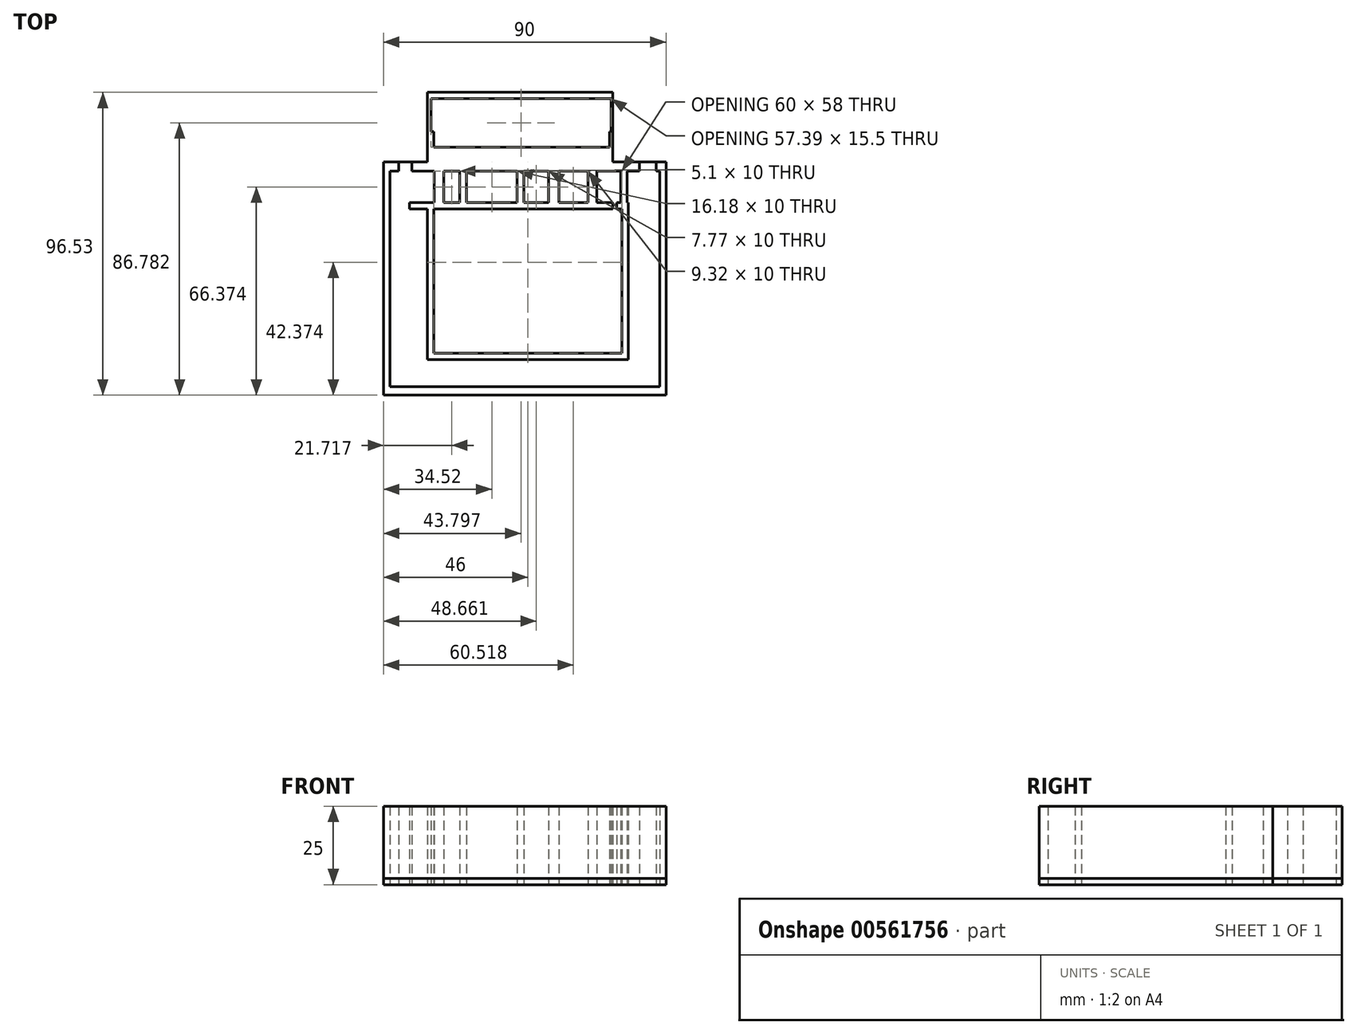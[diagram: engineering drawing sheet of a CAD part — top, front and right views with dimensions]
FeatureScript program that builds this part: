
annotation { "Feature Type Name" : "Feature", "Feature Type Description" : "" }
export const myFeature = defineFeature(function(context is Context, id is Id, definition is map)
    precondition{}
    {
        {
            var Q0;
            Q0=qCreatedBy(makeId("Top.planeOp"),FACE);
            var sketch = newSketch(context, id + "F0", { "sketchPlane" : qUnion([Q0])});
            skLineSegment(sketch, "E0.bottom", {"start": v(-74, 79.03) * mm, "end": v(-62.27, 79.03) * mm, "construction": true});
            skLineSegment(sketch, "E0.top", {"start": v(-62.27, 5.03) * mm, "end": v(-47.4, 5.03) * mm, "construction": true});
            skLineSegment(sketch, "E0.left", {"start": v(-62.27, 79.03) * mm, "end": v(-62.27, 5.03) * mm, "construction": true});
            skLineSegment(sketch, "E1.bottom", {"start": v(-74, 13.37) * mm, "end": v(-14, 13.37) * mm});
            skLineSegment(sketch, "E1.top", {"start": v(-74, 59.37) * mm, "end": v(-22.82, 59.37) * mm});
            skLineSegment(sketch, "E1.left", {"start": v(-74, 13.37) * mm, "end": v(-74, 59.37) * mm});
            skLineSegment(sketch, "E1.right", {"start": v(-14, 13.37) * mm, "end": v(-14, 59.37) * mm});
            skLineSegment(sketch, "E2.bottom", {"start": v(-76, 61.37) * mm, "end": v(-73.89, 61.37) * mm});
            skLineSegment(sketch, "E2.top", {"start": v(-76, 11.37) * mm, "end": v(-12, 11.37) * mm});
            skLineSegment(sketch, "E2.left", {"start": v(-76, 59.37) * mm, "end": v(-76, 11.37) * mm});
            skLineSegment(sketch, "E2.right", {"start": v(-12, 61.37) * mm, "end": v(-12, 11.37) * mm});
            skLineSegment(sketch, "E3", {"start": v(-24.82, 59.37) * mm, "end": v(-24.82, 52.37) * mm});
            skLineSegment(sketch, "E4.top", {"start": v(-32.73, 78.03) * mm, "end": v(-0.73, 78.03) * mm, "construction": true});
            skLineSegment(sketch, "E5", {"start": v(-90, 74.37) * mm, "end": v(-76, 74.37) * mm});
            skLineSegment(sketch, "E6", {"start": v(-74.9, 84.03) * mm, "end": v(-74.9, 94.53) * mm});
            skLineSegment(sketch, "E7", {"start": v(-74.9, 94.53) * mm, "end": v(-17.51, 94.53) * mm});
            skLineSegment(sketch, "E8", {"start": v(-17.51, 94.53) * mm, "end": v(-17.51, 84.03) * mm});
            skLineSegment(sketch, "E9", {"start": v(-17, 74.37) * mm, "end": v(0, 74.37) * mm});
            skLineSegment(sketch, "E10", {"start": v(-22.1, 61.37) * mm, "end": v(-76, 61.37) * mm});
            skLineSegment(sketch, "E11", {"start": v(-7, 31.7) * mm, "end": v(-9.5, 31.7) * mm});
            skLineSegment(sketch, "E12", {"start": v(-9.5, 31.7) * mm, "end": v(-9.5, 34.2) * mm});
            skLineSegment(sketch, "E13", {"start": v(-9.5, 34.2) * mm, "end": v(-7, 34.2) * mm});
            skLineSegment(sketch, "E14", {"start": v(-84.23, 36.5) * mm, "end": v(33.28, 36.5) * mm, "construction": true});
            skLineSegment(sketch, "E15", {"start": v(-17.51, 79.03) * mm, "end": v(-74, 79.03) * mm});
            skLineSegment(sketch, "E16", {"start": v(-17, 74.37) * mm, "end": v(-17, 96.53) * mm});
            skLineSegment(sketch, "E17", {"start": v(-17, 96.53) * mm, "end": v(-76, 96.53) * mm});
            skLineSegment(sketch, "E18", {"start": v(-76, 96.53) * mm, "end": v(-76, 74.37) * mm});
            skLineSegment(sketch, "E19", {"start": v(-15.12, 59.37) * mm, "end": v(-15.12, 52.37) * mm});
            skLineSegment(sketch, "E20", {"start": v(-22.82, 59.37) * mm, "end": v(-22.82, 52.37) * mm});
            skLineSegment(sketch, "E21", {"start": v(-14.4, 61.37) * mm, "end": v(-14.4, 71.37) * mm});
            skLineSegment(sketch, "E22", {"start": v(-22.1, 71.37) * mm, "end": v(-22.1, 61.37) * mm});
            skLineSegment(sketch, "E23.trimOffspring", {"start": v(-12, 61.37) * mm, "end": v(-14.4, 61.37) * mm});
            skLineSegment(sketch, "E24.trimOffspring", {"start": v(-17.64, 59.37) * mm, "end": v(-14, 59.37) * mm});
            skLineSegment(sketch, "E25.trimOffspring", {"start": v(-14.4, 61.37) * mm, "end": v(-12, 61.37) * mm});
            skLineSegment(sketch, "E26", {"start": v(-17.64, 59.37) * mm, "end": v(-22.82, 59.37) * mm});
            skPoint(sketch, "E27.orphan", {"position": v(0, 0) * mm});
            skLineSegment(sketch, "E28", {"start": v(-74, 84.03) * mm, "end": v(-74.9, 84.03) * mm});
            skLineSegment(sketch, "E29", {"start": v(-18, 79.03) * mm, "end": v(-17.51, 79.03) * mm});
            skLineSegment(sketch, "E30", {"start": v(-18, 79.03) * mm, "end": v(-18, 84.03) * mm});
            skLineSegment(sketch, "E31", {"start": v(-74, 84.03) * mm, "end": v(-74, 79.03) * mm});
            skLineSegment(sketch, "E32", {"start": v(-74, 79.03) * mm, "end": v(-74, 79.03) * mm});
            skLineSegment(sketch, "E33", {"start": v(-18, 84.03) * mm, "end": v(-17.51, 84.03) * mm});
            skLineSegment(sketch, "E34", {"start": v(-90, 47) * mm, "end": v(-90, 74.37) * mm});
            skLineSegment(sketch, "E35", {"start": v(-2, 2.73) * mm, "end": v(-2, 71.37) * mm});
            skLineSegment(sketch, "E36", {"start": v(-90, 0) * mm, "end": v(-90, 47) * mm});
            skLineSegment(sketch, "E37", {"start": v(0, 74.37) * mm, "end": v(0, 0) * mm});
            skLineSegment(sketch, "E38", {"start": v(-88, 71.37) * mm, "end": v(-2, 71.37) * mm});
            skLineSegment(sketch, "E39", {"start": v(-74, 52.37) * mm, "end": v(-14, 52.37) * mm});
            skLineSegment(sketch, "E40", {"start": v(-73, 51.37) * mm, "end": v(-22.82, 51.37) * mm});
            skLineSegment(sketch, "E41", {"start": v(-73, 51.37) * mm, "end": v(-73, 14.37) * mm});
            skLineSegment(sketch, "E42", {"start": v(-73, 14.37) * mm, "end": v(-15, 14.37) * mm});
            skLineSegment(sketch, "E43", {"start": v(-15, 14.37) * mm, "end": v(-15, 51.37) * mm});
            skLineSegment(sketch, "E44", {"start": v(-22.82, 52.37) * mm, "end": v(-22.82, 50.37) * mm});
            skLineSegment(sketch, "E45", {"start": v(-22.82, 50.37) * mm, "end": v(-15.12, 50.37) * mm});
            skLineSegment(sketch, "E46", {"start": v(-15.12, 50.37) * mm, "end": v(-15.12, 52.37) * mm});
            skLineSegment(sketch, "E47.trimOffspring", {"start": v(-15.12, 51.37) * mm, "end": v(-15, 51.37) * mm});
            skLineSegment(sketch, "E48", {"start": v(-22.82, 50.37) * mm, "end": v(-73, 50.37) * mm, "construction": true});
            skLineSegment(sketch, "E49", {"start": v(-15.12, 50.37) * mm, "end": v(-15, 50.37) * mm, "construction": true});
            skLineSegment(sketch, "E50", {"start": v(-22.1, 61.37) * mm, "end": v(-14.4, 61.37) * mm});
            skLineSegment(sketch, "E51", {"start": v(-24.82, 61.37) * mm, "end": v(-24.82, 78.03) * mm});
            skLineSegment(sketch, "E52", {"start": v(-12.4, 71.37) * mm, "end": v(-12.4, 61.37) * mm});
            skLineSegment(sketch, "E53", {"start": v(-12, 61.37) * mm, "end": v(-2, 61.37) * mm});
            skLineSegment(sketch, "E54", {"start": v(-12, 59.37) * mm, "end": v(-2, 59.37) * mm});
            skLineSegment(sketch, "E55", {"start": v(-74, 59.37) * mm, "end": v(-88, 59.37) * mm});
            skLineSegment(sketch, "E56", {"start": v(-76, 61.37) * mm, "end": v(-88, 61.37) * mm});
            skLineSegment(sketch, "E57", {"start": v(-73.89, 61.37) * mm, "end": v(-73.89, 71.37) * mm});
            skLineSegment(sketch, "E58", {"start": v(-70.83, 71.37) * mm, "end": v(-70.83, 61.37) * mm});
            skLineSegment(sketch, "E59", {"start": v(-65.74, 71.37) * mm, "end": v(-65.74, 61.37) * mm});
            skLineSegment(sketch, "E60", {"start": v(-63.57, 71.37) * mm, "end": v(-63.57, 61.37) * mm});
            skLineSegment(sketch, "E61", {"start": v(-47.39, 71.37) * mm, "end": v(-47.39, 61.37) * mm});
            skLineSegment(sketch, "E62", {"start": v(-45.22, 71.37) * mm, "end": v(-45.22, 61.37) * mm});
            skLineSegment(sketch, "E63", {"start": v(-37.45, 71.37) * mm, "end": v(-37.45, 61.37) * mm});
            skLineSegment(sketch, "E64", {"start": v(-34.14, 71.37) * mm, "end": v(-34.14, 61.37) * mm});
            skLineSegment(sketch, "E65.trimOffspring", {"start": v(-70.83, 61.37) * mm, "end": v(-65.74, 61.37) * mm});
            skLineSegment(sketch, "E66.trimOffspring", {"start": v(-63.57, 61.37) * mm, "end": v(-47.39, 61.37) * mm});
            skLineSegment(sketch, "E67.trimOffspring", {"start": v(-45.22, 61.37) * mm, "end": v(-37.45, 61.37) * mm});
            skLineSegment(sketch, "E68.trimOffspring", {"start": v(-34.14, 61.37) * mm, "end": v(-22.1, 61.37) * mm});
            skLineSegment(sketch, "E69", {"start": v(-16.94, 61.37) * mm, "end": v(-16.94, 59.37) * mm});
            skLineSegment(sketch, "E70", {"start": v(-81.77, 61.37) * mm, "end": v(-81.77, 59.37) * mm});
            skLineSegment(sketch, "E71", {"start": v(-85.98, 61.37) * mm, "end": v(-85.98, 59.37) * mm});
            skLineSegment(sketch, "E72", {"start": v(-85.18, 74.37) * mm, "end": v(-85.18, 71.37) * mm});
            skLineSegment(sketch, "E73", {"start": v(-80.98, 74.37) * mm, "end": v(-80.98, 71.37) * mm});
            skLineSegment(sketch, "E74", {"start": v(-5.96, 74.37) * mm, "end": v(-5.96, 71.37) * mm});
            skLineSegment(sketch, "E75", {"start": v(-3.17, 74.37) * mm, "end": v(-3.17, 71.37) * mm});
            skLineSegment(sketch, "E76", {"start": v(-88, 71.37) * mm, "end": v(-88, 2.73) * mm});
            skLineSegment(sketch, "E77", {"start": v(-90, 0) * mm, "end": v(0, 0) * mm});
            skLineSegment(sketch, "E78", {"start": v(-88, 2.73) * mm, "end": v(-2, 2.73) * mm});
            skLineSegment(sketch, "E79", {"start": v(-15.63, 61.37) * mm, "end": v(-15.63, 59.37) * mm});
            skLineSegment(sketch, "E80", {"start": v(-82.64, 74.37) * mm, "end": v(-82.64, 71.37) * mm});
            skLineSegment(sketch, "E81", {"start": v(-8.5, 74.37) * mm, "end": v(-8.5, 71.37) * mm});
            skSolve(sketch);
        }
        {
            var Q0;
            {var subQ6=sQuery(id+"F0.wireOp",EDGE,"aaf6255e-d457-4121-a573-c6537bed1f96");Q0=makeQuery(id+"F0.imprint","IMPRINT",FACE,{"disambiguationData":[TD([[makeQuery(id+"F0.imprint","IMPRINT",EDGE,{"derivedFrom":subQ6}),-1.0]])]});}
            var Q1;
            {var subQ3=sQuery(id+"F0.wireOp",EDGE,"5609a195-c4f9-4922-93db-bb14c538a4c4");Q1=makeQuery(id+"F0.imprint","IMPRINT",FACE,{"disambiguationData":[TD([[makeQuery(id+"F0.imprint","IMPRINT",EDGE,{"derivedFrom":subQ3}),1.0]])]});}
            var Q2;
            {var subQ0=sQuery(id+"F0.wireOp",EDGE,"E11");Q2=makeQuery(id+"F0.imprint","IMPRINT",FACE,{"disambiguationData":[TD([[makeQuery(id+"F0.imprint","IMPRINT",EDGE,{"derivedFrom":subQ0}),-1.0]])]});}
            var Q3;
            {var subQ18=sQuery(id+"F0.wireOp",EDGE,"E1.bottom");Q3=makeQuery(id+"F0.imprint","IMPRINT",FACE,{"disambiguationData":[TD([[makeQuery(id+"F0.imprint","IMPRINT",EDGE,{"derivedFrom":subQ18}),-1.0]])]});}
            var Q4;
            Q4=makeQuery(id+"F0.imprint","IMPRINT",FACE,{"disambiguationData":[TD([[makeQuery(id+"F0.imprint","IMPRINT",EDGE,{"derivedFrom":sQuery(id+"F0.wireOp",EDGE,"E6")}),1.0]])]});
            var Q5;
            {var subQ11=sQuery(id+"F0.wireOp",EDGE,"E34");Q5=makeQuery(id+"F0.imprint","IMPRINT",FACE,{"disambiguationData":[TD([[makeQuery(id+"F0.imprint","IMPRINT",EDGE,{"derivedFrom":subQ11}),-1.0]])]});}
            extrude(context, id + "F1", {"entities" : qUnion([Q0, Q1, Q2, Q3, Q4, Q5]), "depth" : 25 * mm, "offsetDistance" : 25 * mm});
        }
        {
            var Q0;
            {var subQ5=sQuery(id+"F0.wireOp",EDGE,"E69");Q0=makeQuery(id+"F0.imprint","IMPRINT",FACE,{"disambiguationData":[TD([[makeQuery(id+"F0.imprint","IMPRINT",EDGE,{"derivedFrom":subQ5}),-1.0]])]});}
            var Q1;
            {var subQ5=sQuery(id+"F0.wireOp",EDGE,"FqiR6hEK-ze8Q-b9ag-ECoh-BVBlXcEPhcP8");Q1=makeQuery(id+"F0.imprint","IMPRINT",FACE,{"disambiguationData":[TD([[makeQuery(id+"F0.imprint","IMPRINT",EDGE,{"derivedFrom":subQ5}),1.0]])]});}
            var Q2;
            {var subQ18=sQuery(id+"F0.wireOp",EDGE,"E1.bottom");Q2=makeQuery(id+"F0.imprint","IMPRINT",FACE,{"disambiguationData":[TD([[makeQuery(id+"F0.imprint","IMPRINT",EDGE,{"derivedFrom":subQ18}),-1.0]])]});}
            var Q3;
            {var subQ0=sQuery(id+"F0.wireOp",EDGE,"E22");Q3=makeQuery(id+"F0.imprint","IMPRINT",FACE,{"disambiguationData":[TD([[makeQuery(id+"F0.imprint","IMPRINT",EDGE,{"derivedFrom":subQ0}),-1.0]])]});}
            var Q4;
            {var subQ0=sQuery(id+"F0.wireOp",EDGE,"E21");Q4=makeQuery(id+"F0.imprint","IMPRINT",FACE,{"disambiguationData":[TD([[makeQuery(id+"F0.imprint","IMPRINT",EDGE,{"derivedFrom":subQ0}),-1.0]])]});}
            var Q5;
            {var subQ2=sQuery(id+"F0.wireOp",EDGE,"E63");Q5=makeQuery(id+"F0.imprint","IMPRINT",FACE,{"disambiguationData":[TD([[makeQuery(id+"F0.imprint","IMPRINT",EDGE,{"derivedFrom":subQ2}),1.0]])]});}
            var Q6;
            {var subQ0=sQuery(id+"F0.wireOp",EDGE,"E61");Q6=makeQuery(id+"F0.imprint","IMPRINT",FACE,{"disambiguationData":[TD([[makeQuery(id+"F0.imprint","IMPRINT",EDGE,{"derivedFrom":subQ0}),1.0]])]});}
            var Q7;
            {var subQ0=sQuery(id+"F0.wireOp",EDGE,"E59");Q7=makeQuery(id+"F0.imprint","IMPRINT",FACE,{"disambiguationData":[TD([[makeQuery(id+"F0.imprint","IMPRINT",EDGE,{"derivedFrom":subQ0}),1.0]])]});}
            var Q8;
            {var subQ0=sQuery(id+"F0.wireOp",EDGE,"E57");Q8=makeQuery(id+"F0.imprint","IMPRINT",FACE,{"disambiguationData":[TD([[makeQuery(id+"F0.imprint","IMPRINT",EDGE,{"derivedFrom":subQ0}),-1.0]])]});}
            extrude(context, id + "F2", {"entities" : qUnion([Q0, Q1, Q2, Q3, Q4, Q5, Q6, Q7, Q8]), "operationType" : NewBodyOperationType.ADD, "depth" : 25 * mm, "offsetDistance" : 25 * mm});
        }
        {
            var Q0;
            Q0=qCreatedBy(makeId("Top.planeOp"),FACE);
            var sketch = newSketch(context, id + "F3", { "sketchPlane" : qUnion([Q0])});
            skLineSegment(sketch, "E82.bottom", {"start": v(0, 0) * mm, "end": v(-90, 0) * mm});
            skLineSegment(sketch, "E82.top", {"start": v(-17, 96.53) * mm, "end": v(-76, 96.53) * mm});
            skLineSegment(sketch, "E82.left", {"start": v(0, 0) * mm, "end": v(0, 74.37) * mm});
            skLineSegment(sketch, "E82.right", {"start": v(-90, 0) * mm, "end": v(-90, 74.37) * mm});
            skLineSegment(sketch, "E83", {"start": v(-76, 96.53) * mm, "end": v(-76, 74.37) * mm});
            skLineSegment(sketch, "E84", {"start": v(-76, 74.37) * mm, "end": v(-90, 74.37) * mm});
            skLineSegment(sketch, "E85", {"start": v(-17, 96.53) * mm, "end": v(-17, 74.37) * mm});
            skLineSegment(sketch, "E86", {"start": v(-17, 74.37) * mm, "end": v(0, 74.37) * mm});
            skSolve(sketch);
        }
        {
            var Q0;
            Q0=qSketchRegion(id+"F3",true);
            extrude(context, id + "F4", {"entities" : qUnion([Q0]), "depth" : 2 * mm, "offsetDistance" : 25 * mm});
        }
    });
